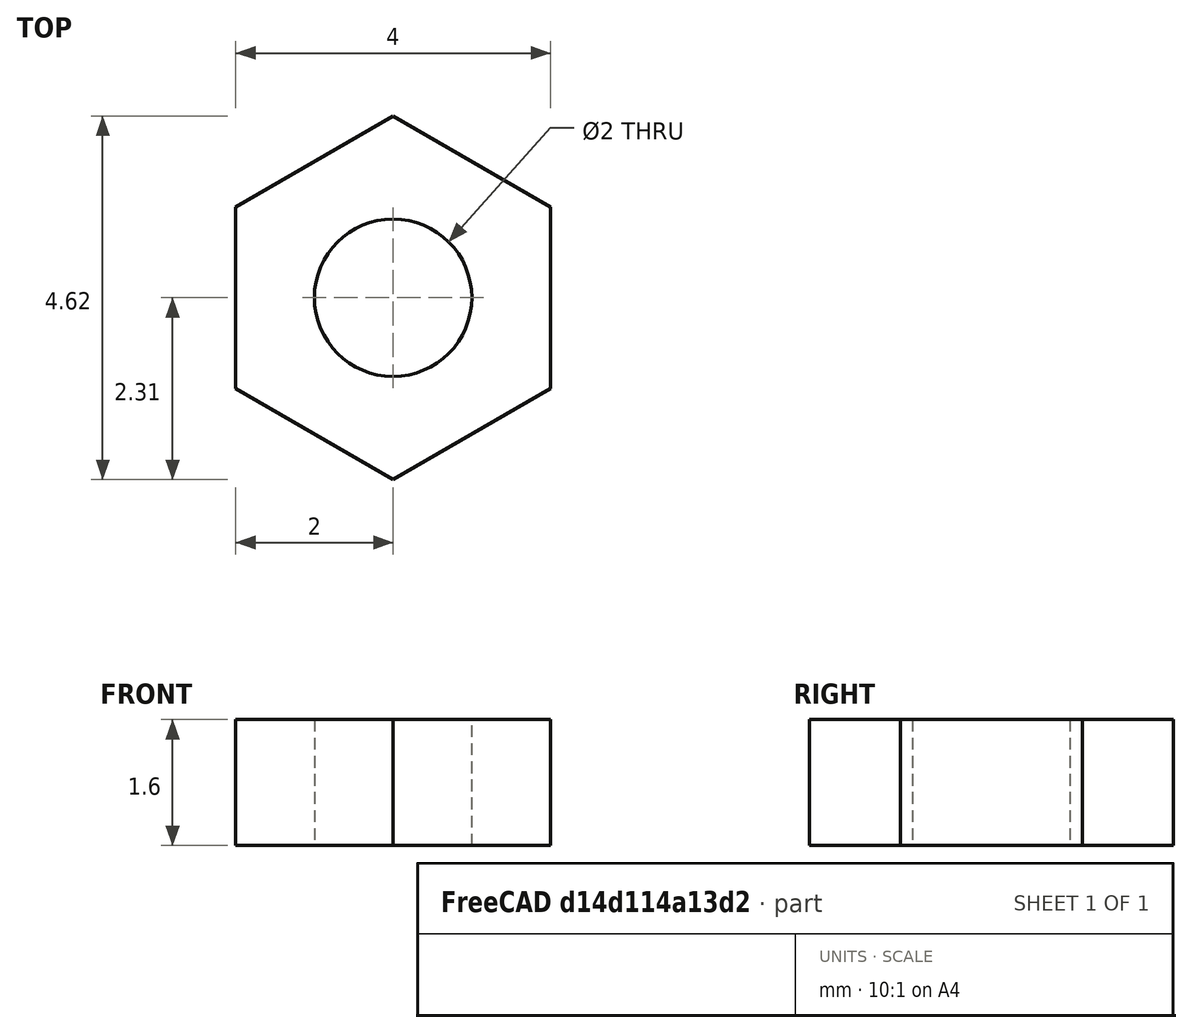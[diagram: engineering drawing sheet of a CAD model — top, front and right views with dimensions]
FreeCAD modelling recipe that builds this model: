
FCSTD DOCUMENT  (FreeCAD 0.18R14555 (Git shallow))
Label: m2-nut
License: All rights reserved
LicenseURL: http://en.wikipedia.org/wiki/All_rights_reserved
objects: Sketcher::SketchObject×1, PartDesign::Pad×1, PartDesign::Body×1
note: 4 computed .brp shape members not serialized (recipe doc carries the construction recipe); baked Part::Feature solids carry a one-line shape summary decoded from their .brp

FEATURE [Sketcher::SketchObject] Sketch
  MapMode = 5
  Support = -> [XY_Plane]
  sketch-geometry (8):
    g0: Circle CenterX=0 CenterY=0 CenterZ=0 NormalX=0 NormalY=0 NormalZ=1 AngleXU=0 Radius=1
    g1: LineSegment StartX=2 StartY=1.1547 StartZ=0 EndX=0 EndY=2.3094 EndZ=0
    g2: LineSegment StartX=1e-16 StartY=2.3094 StartZ=0 EndX=-2 EndY=1.1547 EndZ=0
    g3: LineSegment StartX=-2 StartY=1.1547 StartZ=0 EndX=-2 EndY=-1.1547 EndZ=0
    g4: LineSegment StartX=-2 StartY=-1.1547 StartZ=0 EndX=4e-16 EndY=-2.3094 EndZ=0
    g5: LineSegment StartX=4e-16 StartY=-2.3094 StartZ=0 EndX=2 EndY=-1.1547 EndZ=0
    g6: LineSegment StartX=2 StartY=-1.1547 StartZ=0 EndX=2 EndY=1.1547 EndZ=0
    g7: Circle [constr] CenterX=0 CenterY=0 CenterZ=0 NormalX=0 NormalY=0 NormalZ=1 AngleXU=0 Radius=2.3094
  constraints (18):
    c: Coincident(g0,g-1)
    c: Coincident(g1,g2)
    c: Coincident(g2,g3)
    c: Coincident(g3,g4)
    c: Coincident(g4,g5)
    c: Coincident(g5,g6)
    c: Coincident(g6,g1)
    c: Equal(g1, g2-g6) x5
    c: PointOnObject(g1,g7)
    c: PointOnObject(g2,g7)
    c: PointOnObject(g3,g7)
    c: PointOnObject(g4,g7)
    c: PointOnObject(g5,g7)
    c: PointOnObject(g6,g7)
    c: Coincident(g7,g0)
    c: Vertical(g6)
    c: Radius(g0) = 1
    c: DistanceX(g2,g1) = 4
FEATURE [PartDesign::Pad] Pad
  Length = 1.6
  Length2 = 100
  Profile = -> Sketch
  Type = 0
FEATURE [PartDesign::Body] Body
  Group = -> [Sketch,Pad]
  Origin = -> Origin
  Tip = -> Pad
